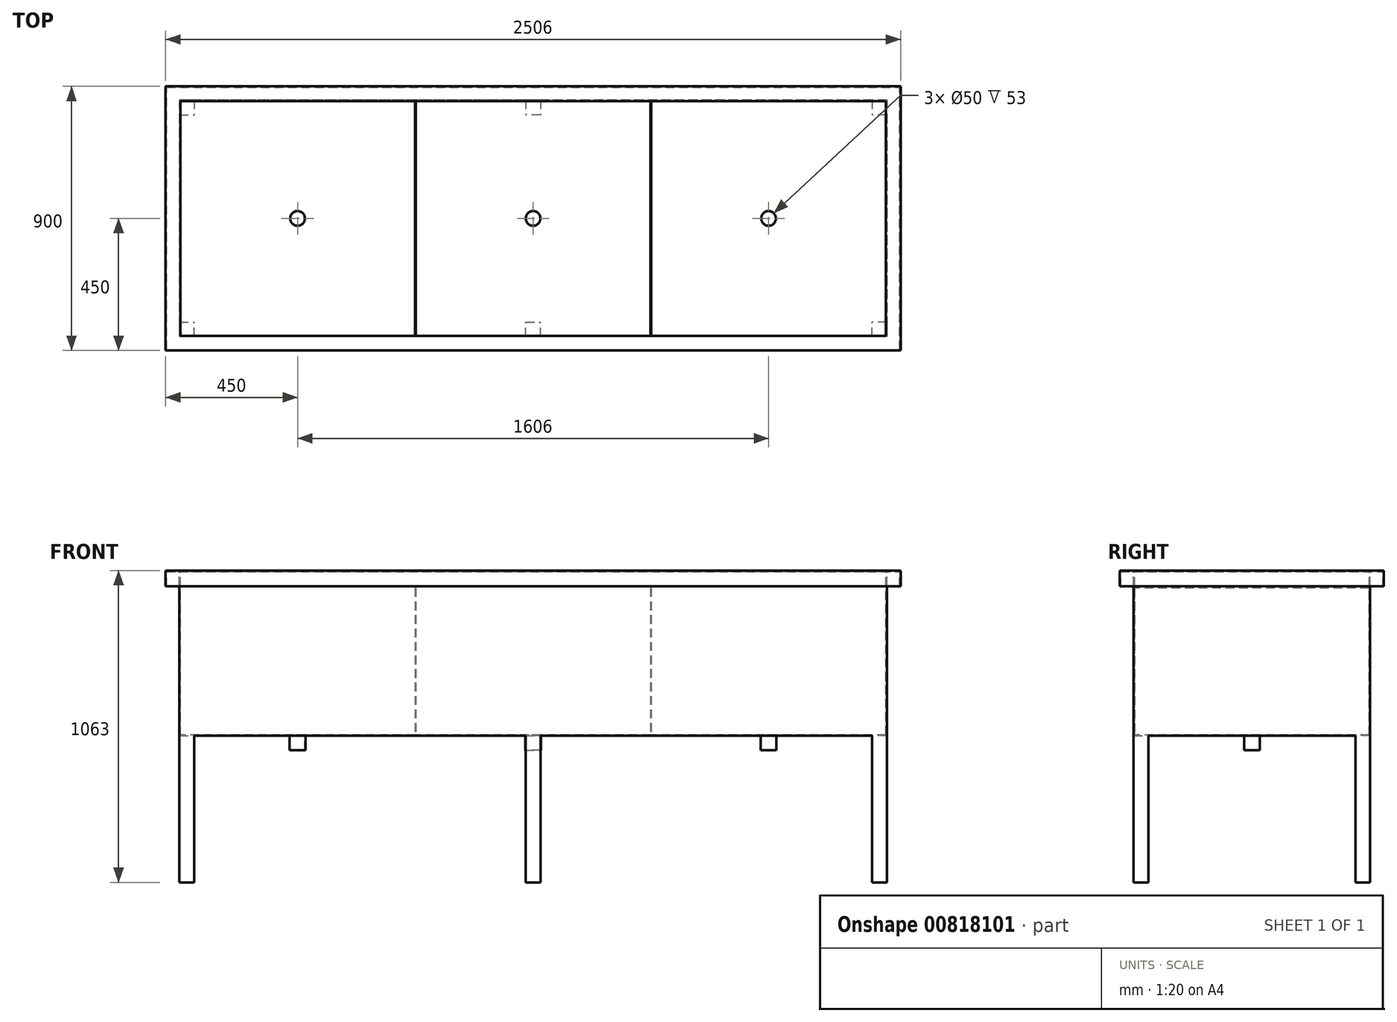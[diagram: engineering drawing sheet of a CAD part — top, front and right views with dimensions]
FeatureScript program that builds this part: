
annotation { "Feature Type Name" : "Feature", "Feature Type Description" : "" }
export const myFeature = defineFeature(function(context is Context, id is Id, definition is map)
    precondition{}
    {
        {
            var Q0;
            Q0=qCreatedBy(makeId("Top.planeOp"),FACE);
            var sketch = newSketch(context, id + "F0", { "sketchPlane" : qUnion([Q0])});
            skLineSegment(sketch, "E0.bottom", {"start": v(0, 0) * mm, "end": v(-2412, 0) * mm});
            skLineSegment(sketch, "E0.top", {"start": v(0, -806) * mm, "end": v(-2412, -806) * mm});
            skLineSegment(sketch, "E0.left", {"start": v(0, 0) * mm, "end": v(0, -806) * mm});
            skLineSegment(sketch, "E0.right", {"start": v(-2412, 0) * mm, "end": v(-2412, -806) * mm});
            skSolve(sketch);
        }
        {
            var Q0;
            Q0=makeQuery(id+"F0.imprint","IMPRINT",FACE,{"disambiguationData":[TD([[makeQuery(id+"F0.imprint","IMPRINT",EDGE,{"derivedFrom":sQuery(id+"F0.wireOp",EDGE,"E0.bottom")}),1.0]])]});
            extrude(context, id + "F1", {"entities" : qUnion([Q0]), "oppositeDirection" : true, "depth" : 563 * mm, "offsetDistance" : 25 * mm});
        }
        {
            var Q0;
            Q0=makeQuery(id+"F1.opExtrude","CAP_FACE",FACE,{"disambiguationData":[OSD([sQuery(id+"F0.wireOp",EDGE,"E0.bottom"),sQuery(id+"F0.wireOp",EDGE,"E0.top"),sQuery(id+"F0.wireOp",EDGE,"E0.left"),sQuery(id+"F0.wireOp",EDGE,"E0.right")])],"isStart":true});
            shell(context, id + "F2", {"entities" : qUnion([Q0]), "thickness" : 3 * mm});
        }
        {
            var Q0;
            Q0=makeQuery(id+"F2.opShell","OFFSET_FACE",FACE,{"disambiguationData":[OSD([sQuery(id+"F0.wireOp",EDGE,"E0.bottom"),sQuery(id+"F0.wireOp",EDGE,"E0.top"),sQuery(id+"F0.wireOp",EDGE,"E0.left"),sQuery(id+"F0.wireOp",EDGE,"E0.right")])]});
            var sketch = newSketch(context, id + "F3", { "sketchPlane" : qUnion([Q0])});
            skLineSegment(sketch, "E1.bottom", {"start": v(-1609, -3) * mm, "end": v(-1606, -3) * mm});
            skLineSegment(sketch, "E1.top", {"start": v(-1609, -803) * mm, "end": v(-1606, -803) * mm});
            skLineSegment(sketch, "E1.left", {"start": v(-1609, -3) * mm, "end": v(-1609, -803) * mm});
            skLineSegment(sketch, "E1.right", {"start": v(-1606, -3) * mm, "end": v(-1606, -803) * mm});
            skLineSegment(sketch, "E2.bottom", {"start": v(-806, -3) * mm, "end": v(-803, -3) * mm});
            skLineSegment(sketch, "E2.top", {"start": v(-806, -803) * mm, "end": v(-803, -803) * mm});
            skLineSegment(sketch, "E2.left", {"start": v(-806, -3) * mm, "end": v(-806, -803) * mm});
            skLineSegment(sketch, "E2.right", {"start": v(-803, -3) * mm, "end": v(-803, -803) * mm});
            skSolve(sketch);
        }
        {
            var Q0;
            Q0 = qSketchRegion(id + "F3", true);
            extrude(context, id + "F4", {"entities" : qUnion([Q0]), "operationType" : NewBodyOperationType.ADD, "depth" : 500 * mm, "offsetDistance" : 25 * mm});
        }
        {
            var Q0;
            Q0=makeQuery(id+"F1.opExtrude","CAP_FACE",FACE,{"disambiguationData":[OSD([sQuery(id+"F0.wireOp",EDGE,"E0.bottom"),sQuery(id+"F0.wireOp",EDGE,"E0.top"),sQuery(id+"F0.wireOp",EDGE,"E0.left"),sQuery(id+"F0.wireOp",EDGE,"E0.right")])],"isStart":true});
            var sketch = newSketch(context, id + "F5", { "sketchPlane" : qUnion([Q0])});
            skLineSegment(sketch, "E3.bottom", {"start": v(47, 47) * mm, "end": v(-2459, 47) * mm});
            skLineSegment(sketch, "E3.top", {"start": v(47, -853) * mm, "end": v(-2459, -853) * mm});
            skLineSegment(sketch, "E3.left", {"start": v(47, 47) * mm, "end": v(47, -853) * mm});
            skLineSegment(sketch, "E3.right", {"start": v(-2459, 47) * mm, "end": v(-2459, -853) * mm});
            skSolve(sketch);
        }
        {
            var Q0;
            Q0=makeQuery(id+"F5.imprint","IMPRINT",FACE,{"disambiguationData":[TD([[makeQuery(id+"F5.imprint","IMPRINT",EDGE,{"derivedFrom":sQuery(id+"F5.wireOp",EDGE,"E3.bottom")}),1.0]])]});
            extrude(context, id + "F6", {"entities" : qUnion([Q0]), "operationType" : NewBodyOperationType.ADD, "oppositeDirection" : true, "depth" : 4 * mm, "offsetDistance" : 25 * mm});
        }
        {
            var Q0;
            {var subQ0=sQuery(id+"F3.wireOp",EDGE,"E1.left");Q0=makeQuery(id+"F3.imprint","IMPRINT",FACE,{"disambiguationData":[TD([[makeQuery(id+"F3.imprint","IMPRINT",EDGE,{"derivedFrom":subQ0}),-1.0]])]});}
            var sketch = newSketch(context, id + "F7", { "sketchPlane" : qUnion([Q0])});
            skCircle(sketch, "E4", {"center": v(-2009, -403) * mm, "radius": 25 * mm});
            skCircle(sketch, "E5", {"center": v(-1206, -403) * mm, "radius": 25 * mm});
            skCircle(sketch, "E6", {"center": v(-403, -403) * mm, "radius": 25 * mm});
            skSolve(sketch);
        }
        {
            var Q0;
            Q0 = qSketchRegion(id + "F7", true);
            extrude(context, id + "F8", {"entities" : qUnion([Q0]), "operationType" : NewBodyOperationType.REMOVE, "oppositeDirection" : true, "depth" : 25 * mm, "offsetDistance" : 25 * mm});
        }
        {
            var Q0;
            Q0=makeQuery(id+"F1.opExtrude","CAP_FACE",FACE,{"disambiguationData":[OSD([sQuery(id+"F0.wireOp",EDGE,"E0.bottom"),sQuery(id+"F0.wireOp",EDGE,"E0.top"),sQuery(id+"F0.wireOp",EDGE,"E0.left"),sQuery(id+"F0.wireOp",EDGE,"E0.right")])],"isStart":false});
            var sketch = newSketch(context, id + "F9", { "sketchPlane" : qUnion([Q0])});
            skCircle(sketch, "E7", {"center": v(-2009, 403) * mm, "radius": 27 * mm});
            skCircle(sketch, "E8", {"center": v(-1206, 403) * mm, "radius": 27 * mm});
            skCircle(sketch, "E9", {"center": v(-403, 403) * mm, "radius": 27 * mm});
            skSolve(sketch);
        }
        {
            var Q0;
            Q0=makeQuery(id+"F9.imprint","IMPRINT",FACE,{"disambiguationData":[TD([[makeQuery(id+"F9.imprint","IMPRINT",EDGE,{"derivedFrom":sQuery(id+"F9.wireOp",EDGE,"E8")}),1.0]])]});
            var Q1;
            Q1=makeQuery(id+"F9.imprint","IMPRINT",FACE,{"disambiguationData":[TD([[makeQuery(id+"F9.imprint","IMPRINT",EDGE,{"derivedFrom":sQuery(id+"F9.wireOp",EDGE,"E7")}),1.0]])]});
            var Q2;
            Q2=makeQuery(id+"F9.imprint","IMPRINT",FACE,{"disambiguationData":[TD([[makeQuery(id+"F9.imprint","IMPRINT",EDGE,{"derivedFrom":sQuery(id+"F9.wireOp",EDGE,"E9")}),1.0]])]});
            extrude(context, id + "F10", {"entities" : qUnion([Q0, Q1, Q2]), "operationType" : NewBodyOperationType.ADD, "depth" : 50 * mm, "offsetDistance" : 25 * mm});
        }
        {
            var Q0;
            Q0=makeQuery(id+"F6.opExtrude","CAP_FACE",FACE,{"disambiguationData":[OSD([sQuery(id+"F0.wireOp",EDGE,"E0.bottom"),sQuery(id+"F0.wireOp",EDGE,"E0.top"),sQuery(id+"F0.wireOp",EDGE,"E0.left"),sQuery(id+"F0.wireOp",EDGE,"E0.right"),sQuery(id+"F5.wireOp",EDGE,"E3.bottom"),sQuery(id+"F5.wireOp",EDGE,"E3.top"),sQuery(id+"F5.wireOp",EDGE,"E3.left"),sQuery(id+"F5.wireOp",EDGE,"E3.right")])],"isStart":false});
            var sketch = newSketch(context, id + "F11", { "sketchPlane" : qUnion([Q0])});
            skLineSegment(sketch, "E10.bottom", {"start": v(47, -47) * mm, "end": v(-2459, -47) * mm});
            skLineSegment(sketch, "E10.top", {"start": v(47, 853) * mm, "end": v(-2459, 853) * mm});
            skLineSegment(sketch, "E10.left", {"start": v(47, -47) * mm, "end": v(47, 853) * mm});
            skLineSegment(sketch, "E10.right", {"start": v(-2459, -47) * mm, "end": v(-2459, 853) * mm});
            skLineSegment(sketch, "E11.bottom", {"start": v(-2456, 850) * mm, "end": v(44, 850) * mm});
            skLineSegment(sketch, "E11.top", {"start": v(-2456, -44) * mm, "end": v(44, -44) * mm});
            skLineSegment(sketch, "E11.left", {"start": v(-2456, 850) * mm, "end": v(-2456, -44) * mm});
            skLineSegment(sketch, "E11.right", {"start": v(44, 850) * mm, "end": v(44, -44) * mm});
            skSolve(sketch);
        }
        {
            var Q0;
            Q0=makeQuery(id+"F11.imprint","IMPRINT",FACE,{"disambiguationData":[TD([[makeQuery(id+"F11.imprint","IMPRINT",EDGE,{"derivedFrom":sQuery(id+"F11.wireOp",EDGE,"E10.bottom")}),-1.0]])]});
            extrude(context, id + "F12", {"entities" : qUnion([Q0]), "operationType" : NewBodyOperationType.ADD, "depth" : 50 * mm, "offsetDistance" : 25 * mm});
        }
        {
            var Q0;
            Q0=makeQuery(id+"F9.imprint","IMPRINT",FACE,{"disambiguationData":[TD([[makeQuery(id+"F9.imprint","IMPRINT",EDGE,{"derivedFrom":sQuery(id+"F9.wireOp",EDGE,"E7")}),-1.0]])]});
            var sketch = newSketch(context, id + "F13", { "sketchPlane" : qUnion([Q0])});
            skLineSegment(sketch, "E12.bottom", {"start": v(-2412, 806) * mm, "end": v(-2362, 806) * mm});
            skLineSegment(sketch, "E12.top", {"start": v(-2412, 756) * mm, "end": v(-2362, 756) * mm});
            skLineSegment(sketch, "E12.left", {"start": v(-2412, 806) * mm, "end": v(-2412, 756) * mm});
            skLineSegment(sketch, "E12.right", {"start": v(-2362, 806) * mm, "end": v(-2362, 756) * mm});
            skLineSegment(sketch, "E13.bottom", {"start": v(-2412, 0) * mm, "end": v(-2362, 0) * mm});
            skLineSegment(sketch, "E13.top", {"start": v(-2412, 50) * mm, "end": v(-2362, 50) * mm});
            skLineSegment(sketch, "E13.left", {"start": v(-2412, 0) * mm, "end": v(-2412, 50) * mm});
            skLineSegment(sketch, "E13.right", {"start": v(-2362, 0) * mm, "end": v(-2362, 50) * mm});
            skLineSegment(sketch, "E14.bottom", {"start": v(0, 806) * mm, "end": v(-50, 806) * mm});
            skLineSegment(sketch, "E14.top", {"start": v(0, 756) * mm, "end": v(-50, 756) * mm});
            skLineSegment(sketch, "E14.left", {"start": v(0, 806) * mm, "end": v(0, 756) * mm});
            skLineSegment(sketch, "E14.right", {"start": v(-50, 806) * mm, "end": v(-50, 756) * mm});
            skLineSegment(sketch, "E15.bottom", {"start": v(0, 0) * mm, "end": v(-50, 0) * mm});
            skLineSegment(sketch, "E15.top", {"start": v(0, 50) * mm, "end": v(-50, 50) * mm});
            skLineSegment(sketch, "E15.left", {"start": v(0, 0) * mm, "end": v(0, 50) * mm});
            skLineSegment(sketch, "E15.right", {"start": v(-50, 0) * mm, "end": v(-50, 50) * mm});
            skLineSegment(sketch, "E16.bottom", {"start": v(-1231, 806) * mm, "end": v(-1181, 806) * mm});
            skLineSegment(sketch, "E16.top", {"start": v(-1231, 756) * mm, "end": v(-1181, 756) * mm});
            skLineSegment(sketch, "E16.left", {"start": v(-1231, 806) * mm, "end": v(-1231, 756) * mm});
            skLineSegment(sketch, "E16.right", {"start": v(-1181, 806) * mm, "end": v(-1181, 756) * mm});
            skLineSegment(sketch, "E17.bottom", {"start": v(-1181, 0) * mm, "end": v(-1231, 0) * mm});
            skLineSegment(sketch, "E17.top", {"start": v(-1181, 50) * mm, "end": v(-1231, 50) * mm});
            skLineSegment(sketch, "E17.left", {"start": v(-1181, 0) * mm, "end": v(-1181, 50) * mm});
            skLineSegment(sketch, "E17.right", {"start": v(-1231, 0) * mm, "end": v(-1231, 50) * mm});
            skSolve(sketch);
        }
        {
            var Q0;
            Q0 = qSketchRegion(id + "F13", true);
            extrude(context, id + "F14", {"entities" : qUnion([Q0]), "operationType" : NewBodyOperationType.ADD, "depth" : 500 * mm, "offsetDistance" : 25 * mm});
        }
    });
